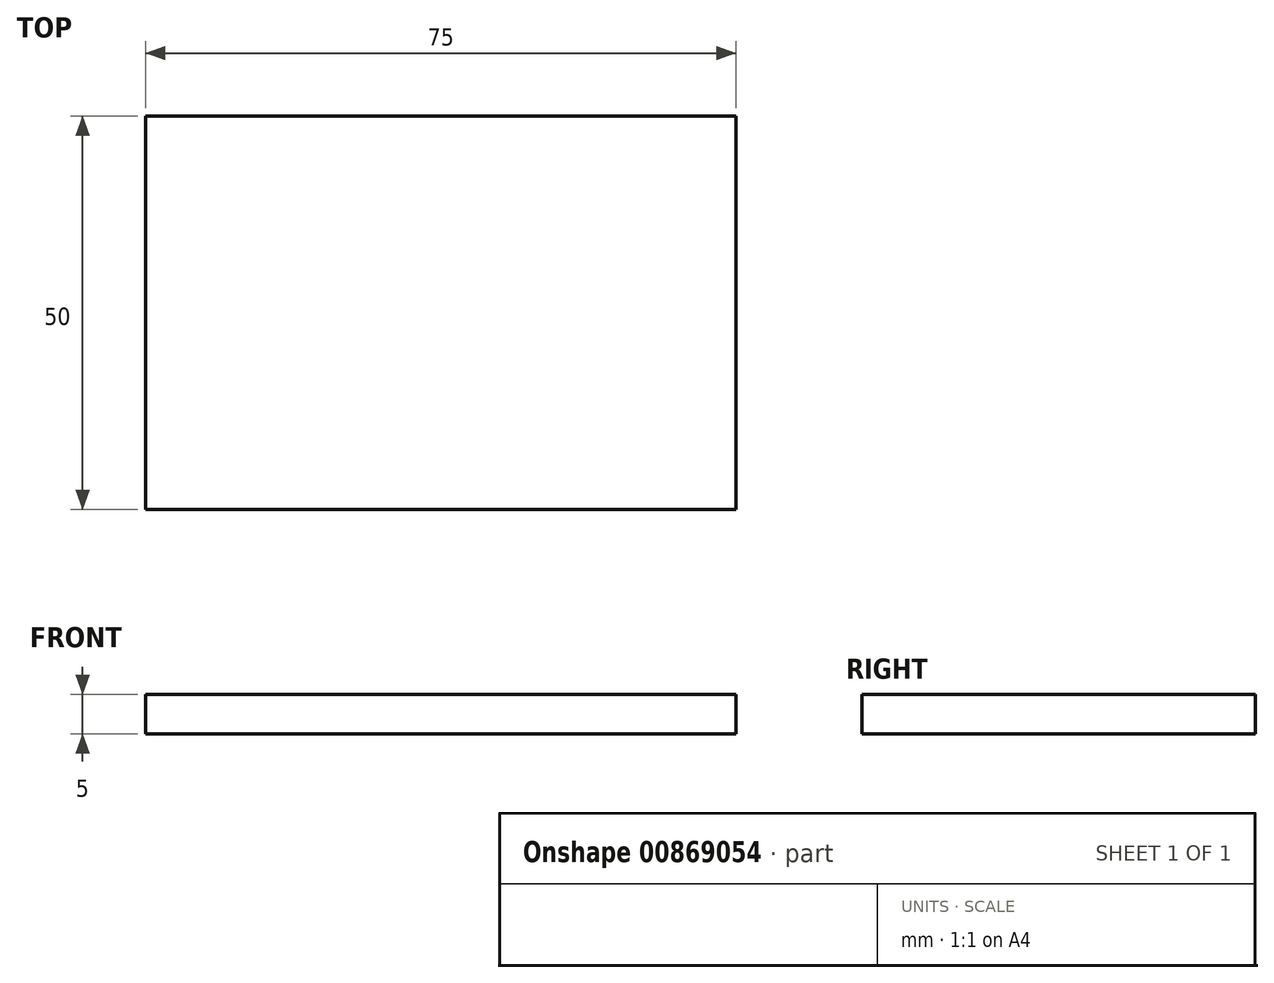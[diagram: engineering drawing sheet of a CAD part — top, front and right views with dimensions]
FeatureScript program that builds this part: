
annotation { "Feature Type Name" : "Feature", "Feature Type Description" : "" }
export const myFeature = defineFeature(function(context is Context, id is Id, definition is map)
    precondition{}
    {
        {
            var Q0;
            Q0=qCreatedBy(makeId("Top.planeOp"),FACE);
            var sketch = newSketch(context, id + "F0", { "sketchPlane" : qUnion([Q0])});
            skLineSegment(sketch, "E0.bottom", {"start": v(0, 0) * mm, "end": v(75, 0) * mm});
            skLineSegment(sketch, "E0.top", {"start": v(0, -50) * mm, "end": v(75, -50) * mm});
            skLineSegment(sketch, "E0.left", {"start": v(0, 0) * mm, "end": v(0, -50) * mm});
            skLineSegment(sketch, "E0.right", {"start": v(75, 0) * mm, "end": v(75, -50) * mm});
            skSolve(sketch);
        }
        {
            var Q0;
            Q0=makeQuery(id+"F0.imprint","IMPRINT",FACE,{"disambiguationData":[TD([[makeQuery(id+"F0.imprint","IMPRINT",EDGE,{"derivedFrom":sQuery(id+"F0.wireOp",EDGE,"E0.bottom")}),-1.0]])]});
            extrude(context, id + "F1", {"entities" : qUnion([Q0]), "depth" : 5 * mm, "offsetDistance" : 25 * mm});
        }
    });
